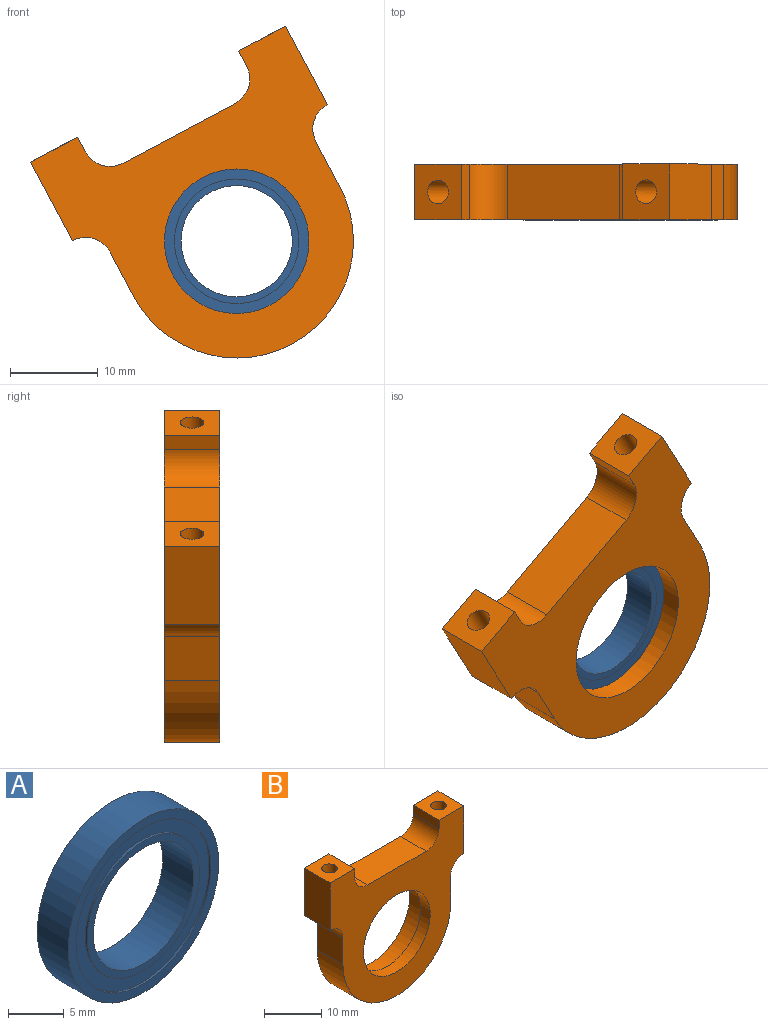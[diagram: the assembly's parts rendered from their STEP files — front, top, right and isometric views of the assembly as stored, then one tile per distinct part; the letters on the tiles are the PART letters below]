
ASSEMBLY  parts=2 mates=1
PART A: 12 faces, bbox 19.1x3.9x19.1 mm
  f0: cylinder r=7.11mm len=14.22mm, axis (0,-1,0), area 11.4mm2, adj f6,f11
  f1: cylinder r=8.55mm len=17.09mm, axis (0,-1,0), area 13.6mm2, adj f9,f11
  f2: cylinder r=7.11mm len=14.22mm, axis (0,1,0), area 11.4mm2, adj f7,f10
  f3: cylinder r=8.55mm len=17.09mm, axis (0,1,0), area 13.6mm2, adj f8,f10
  f4: cylinder r=6.35mm len=12.7mm, axis (0,-1,0), area 156.1mm2, adj f6,f7
  f5: cylinder r=9.53mm len=19.05mm, axis (0,-1,0), area 234.1mm2, adj f8,f9
  f6: plane 14.22x14.22mm, normal (0,-1,0), area 32.2mm2, adj f0,f4
  f7: plane 14.22x14.22mm, normal (0,1,0), area 32.2mm2, adj f2,f4
  f8: plane 19.05x19.05mm, normal (0,1,0), area 55.5mm2, adj f3,f5
  f9: plane 19.05x19.05mm, normal (0,-1,0), area 55.5mm2, adj f1,f5
  f10: plane 17.09x17.09mm, normal (0,1,0), area 70.6mm2, adj f2,f3
  f11: plane 17.09x17.09mm, normal (0,-1,0), area 70.6mm2, adj f0,f1
PART B: 23 faces, bbox 33x6.4x32.4 mm
  f0: cylinder r=8.26mm len=16.51mm, axis (0,1,0), area 123.8mm2, adj f17,f22
  f1: cylinder r=9.53mm len=19.05mm, axis (0,1,0), area 237.1mm2, adj f16,f22
  f2: cylinder r=1.35mm len=7.62mm, axis (0,0,1), area 64.8mm2, adj f3,f9
  f3: cone r=1.35mm half-angle=59deg, axis (0,0,1), area 6.7mm2, adj f2
  f4: cylinder r=1.35mm len=7.62mm, axis (0,0,1), area 64.8mm2, adj f5,f13
  f5: cone r=1.35mm half-angle=59deg, axis (0,0,1), area 6.7mm2, adj f4
  f6: cylinder r=13.33mm len=26.67mm, axis (0,-1,0), area 266mm2, adj f7,f15,f16,f17
  f7: plane 6.35x5.72mm, normal (-1,0,0), area 36.3mm2, adj f6,f16,f17,f18
  f8: plane 10.16x6.35mm, normal (-1,0,0), area 64.5mm2, adj f9,f16,f17,f18
  f9: plane 6.35x6.08mm, normal (0,0,1), area 32.9mm2, adj f2,f8,f10,f16,f17
  f10: plane 6.35x1.91mm, normal (1,0,0), area 12.1mm2, adj f9,f16,f17,f21
  f11: plane 14.51x6.35mm, normal (0,0,1), area 92.1mm2, adj f16,f17,f20,f21
  f12: plane 6.35x1.91mm, normal (-1,0,0), area 12.1mm2, adj f13,f16,f17,f20
  f13: plane 6.35x6.08mm, normal (0,0,1), area 32.9mm2, adj f4,f12,f14,f16,f17
  f14: plane 10.16x6.35mm, normal (1,0,0), area 64.5mm2, adj f13,f16,f17,f19
  f15: plane 6.35x5.72mm, normal (1,0,0), area 36.3mm2, adj f6,f16,f17,f19
  f16: plane 33.02x32.39mm, normal (0,1,0), area 469.6mm2, adj f1,f6,f7,f8,f9,f10,f11,f12
  f17: plane 33.02x32.39mm, normal (0,-1,0), area 540.5mm2, adj f0,f6,f7,f8,f9,f10,f11,f12
  f18: cylinder r=3.17mm len=6.35mm, axis (0,1,0), area 31.7mm2, adj f7,f8,f16,f17
  f19: cylinder r=3.17mm len=6.35mm, axis (0,1,0), area 31.7mm2, adj f14,f15,f16,f17
  f20: cylinder r=3.17mm len=6.35mm, axis (0,1,0), area 31.7mm2, adj f11,f12,f16,f17
  f21: cylinder r=3.17mm len=6.35mm, axis (0,1,0), area 31.7mm2, adj f10,f11,f16,f17
  f22: plane 19.05x19.05mm, normal (0,1,0), area 70.9mm2, adj f0,f1
PLACE A rot(axis=(0,-1,0),118.1deg) t=(9.98,15.5,24.37)mm
PLACE B rot(axis=(0,-1,0),28.1deg) t=(9.98,13.11,24.37)mm
MATE fastened B.f0 <-> A.f0  axis (0,1,0) through (9.98,15.5,24.37)mm
